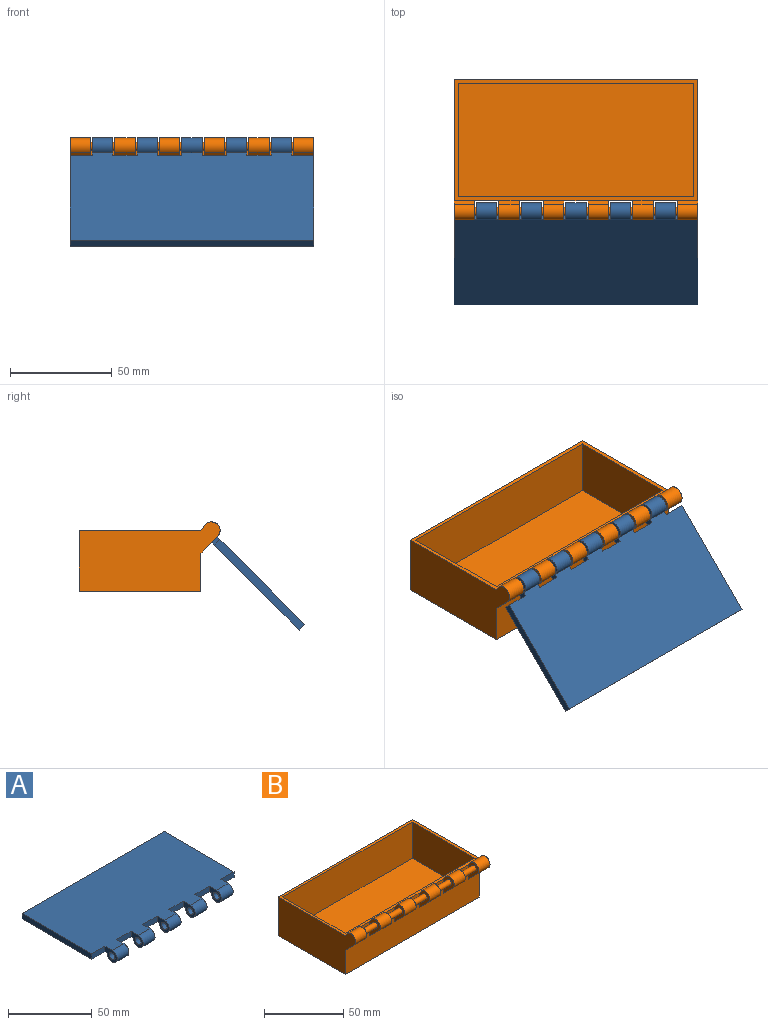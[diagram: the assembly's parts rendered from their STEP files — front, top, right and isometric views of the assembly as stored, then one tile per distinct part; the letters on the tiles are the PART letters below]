
ASSEMBLY  parts=2 mates=1
PART A: 31 faces, bbox 120x69.4x8.4 mm
  f0: plane 10.27x8.4mm, normal (1,0,0), area 48.6mm2, adj f2,f3,f4,f5,f11
  f1: plane 10.27x8.4mm, normal (-1,0,0), area 48.6mm2, adj f2,f3,f4,f5,f6
  f2: plane 120x65.2mm, normal (0,0,1), area 7399.1mm2, adj f0,f1,f3,f6,f7,f8,f9,f11
  f3: cylinder r=4.2mm len=10mm, axis (-1,0,0), area 199.9mm2, adj f0,f1,f2,f4
  f4: plane 120x61mm, normal (0,0,-1), area 7189.4mm2, adj f0,f1,f3,f6,f7,f8,f9,f11
  f5: cylinder r=2.4mm len=10mm, axis (-1,0,0), area 150.8mm2, adj f0,f1
  f6: plane 11x4mm, normal (0,-1,0), area 44mm2, adj f1,f2,f4,f29
  f7: plane 10.27x8.4mm, normal (1,0,0), area 48.6mm2, adj f2,f4,f9,f10,f16
  f8: plane 10.27x8.4mm, normal (-1,0,0), area 48.6mm2, adj f2,f4,f9,f10,f11
  f9: cylinder r=4.2mm len=10mm, axis (-1,0,0), area 199.9mm2, adj f2,f4,f7,f8
  f10: cylinder r=2.4mm len=10mm, axis (-1,0,0), area 150.8mm2, adj f7,f8
  f11: plane 12x4mm, normal (0,-1,0), area 48mm2, adj f0,f2,f4,f8
  f12: plane 10.27x8.4mm, normal (1,0,0), area 48.6mm2, adj f2,f4,f14,f15,f21
  f13: plane 10.27x8.4mm, normal (-1,0,0), area 48.6mm2, adj f2,f4,f14,f15,f16
  f14: cylinder r=4.2mm len=10mm, axis (-1,0,0), area 199.9mm2, adj f2,f4,f12,f13
  f15: cylinder r=2.4mm len=10mm, axis (-1,0,0), area 150.8mm2, adj f12,f13
  f16: plane 12x4mm, normal (0,-1,0), area 48mm2, adj f2,f4,f7,f13
  f17: plane 10.27x8.4mm, normal (1,0,0), area 48.6mm2, adj f2,f4,f19,f20,f26
  f18: plane 10.27x8.4mm, normal (-1,0,0), area 48.6mm2, adj f2,f4,f19,f20,f21
  f19: cylinder r=4.2mm len=10mm, axis (-1,0,0), area 199.9mm2, adj f2,f4,f17,f18
  f20: cylinder r=2.4mm len=10mm, axis (-1,0,0), area 150.8mm2, adj f17,f18
  f21: plane 12x4mm, normal (0,-1,0), area 48mm2, adj f2,f4,f12,f18
  f22: plane 10.27x8.4mm, normal (1,0,0), area 48.6mm2, adj f2,f4,f24,f25,f28
  f23: plane 10.27x8.4mm, normal (-1,0,0), area 48.6mm2, adj f2,f4,f24,f25,f26
  f24: cylinder r=4.2mm len=10mm, axis (-1,0,0), area 199.9mm2, adj f2,f4,f22,f23
  f25: cylinder r=2.4mm len=10mm, axis (-1,0,0), area 150.8mm2, adj f22,f23
  f26: plane 12x4mm, normal (0,-1,0), area 48mm2, adj f2,f4,f17,f23
  f27: plane 59.13x4mm, normal (1,0,0), area 236.5mm2, adj f2,f4,f28,f30
  f28: plane 11x4mm, normal (0,-1,0), area 44mm2, adj f2,f4,f22,f27
  f29: plane 59.13x4mm, normal (-1,0,0), area 236.5mm2, adj f2,f4,f6,f30
  f30: plane 120x4mm, normal (0,1,0), area 480mm2, adj f2,f4,f27,f29
PART B: 44 faces, bbox 120x69.4x34.2 mm
  f0: plane 120x30mm, normal (0,-1,0), area 2931.6mm2, adj f1,f2,f4,f5,f12,f14,f18,f20
  f1: plane 120x60mm, normal (0,0,1), area 704mm2, adj f0,f2,f3,f4,f6,f7,f8,f9
  f2: plane 69.4x34.2mm, normal (1,0,0), area 1888.7mm2, adj f0,f1,f3,f5,f11,f12,f13
  f3: plane 120x30mm, normal (0,1,0), area 3600mm2, adj f1,f2,f4,f5
  f4: plane 69.4x34.2mm, normal (-1,0,0), area 1888.7mm2, adj f0,f1,f3,f5,f40,f41,f42
  f5: plane 120x60mm, normal (0,0,-1), area 7200mm2, adj f0,f2,f3,f4
  f6: plane 116x28mm, normal (0,1,0), area 3248mm2, adj f1,f7,f9,f10
  f7: plane 56x28mm, normal (-1,0,0), area 1568mm2, adj f1,f6,f8,f10
  f8: plane 116x28mm, normal (0,-1,0), area 3248mm2, adj f1,f7,f9,f10
  f9: plane 56x28mm, normal (1,0,0), area 1568mm2, adj f1,f6,f8,f10
  f10: plane 116x56mm, normal (0,0,1), area 6496mm2, adj f6,f7,f8,f9
  f11: cylinder r=4.2mm len=10mm, axis (1,0,0), area 138.4mm2, adj f2,f12,f13,f14
  f12: plane 10x8.17mm, normal (0,-0.71,-0.71), area 115.5mm2, adj f0,f2,f11,f14
  f13: plane 10x2.48mm, normal (0,0.81,0.59), area 30.7mm2, adj f1,f2,f11,f14
  f14: plane 15.34x9.4mm, normal (-1,0,0), area 76.2mm2, adj f0,f11,f12,f13,f15
  f15: cylinder r=2mm len=12mm, axis (1,0,0), area 150.8mm2, adj f14,f21
  f16: cylinder r=2mm len=12mm, axis (1,0,0), area 150.8mm2, adj f20,f26
  f17: cylinder r=4.2mm len=10mm, axis (1,0,0), area 138.4mm2, adj f18,f19,f20,f21
  f18: plane 10x8.17mm, normal (0,-0.71,-0.71), area 115.5mm2, adj f0,f17,f20,f21
  f19: plane 10x2.48mm, normal (0,0.81,0.59), area 30.7mm2, adj f1,f17,f20,f21
  f20: plane 15.34x9.4mm, normal (-1,0,0), area 76.2mm2, adj f0,f16,f17,f18,f19
  f21: plane 15.34x9.4mm, normal (1,0,0), area 76.2mm2, adj f0,f15,f17,f18,f19
  f22: cylinder r=4.2mm len=10mm, axis (1,0,0), area 138.4mm2, adj f23,f24,f25,f26
  f23: plane 10x8.17mm, normal (0,-0.71,-0.71), area 115.5mm2, adj f0,f22,f25,f26
  f24: plane 10x2.48mm, normal (0,0.81,0.59), area 30.7mm2, adj f1,f22,f25,f26
  f25: plane 15.34x9.4mm, normal (-1,0,0), area 76.2mm2, adj f0,f22,f23,f24,f27
  f26: plane 15.34x9.4mm, normal (1,0,0), area 76.2mm2, adj f0,f16,f22,f23,f24
  f27: cylinder r=2mm len=12mm, axis (1,0,0), area 150.8mm2, adj f25,f32
  f28: cylinder r=4.2mm len=10mm, axis (1,0,0), area 138.4mm2, adj f29,f30,f31,f32
  f29: plane 10x8.17mm, normal (0,-0.71,-0.71), area 115.5mm2, adj f0,f28,f31,f32
  f30: plane 10x2.48mm, normal (0,0.81,0.59), area 30.7mm2, adj f1,f28,f31,f32
  f31: plane 15.34x9.4mm, normal (-1,0,0), area 76.2mm2, adj f0,f28,f29,f30,f33
  f32: plane 15.34x9.4mm, normal (1,0,0), area 76.2mm2, adj f0,f27,f28,f29,f30
  f33: cylinder r=2mm len=12mm, axis (1,0,0), area 150.8mm2, adj f31,f38
  f34: cylinder r=4.2mm len=10mm, axis (1,0,0), area 138.4mm2, adj f35,f36,f37,f38
  f35: plane 10x8.17mm, normal (0,-0.71,-0.71), area 115.5mm2, adj f0,f34,f37,f38
  f36: plane 10x2.48mm, normal (0,0.81,0.59), area 30.7mm2, adj f1,f34,f37,f38
  f37: plane 15.34x9.4mm, normal (-1,0,0), area 76.2mm2, adj f0,f34,f35,f36,f39
  f38: plane 15.34x9.4mm, normal (1,0,0), area 76.2mm2, adj f0,f33,f34,f35,f36
  f39: cylinder r=2mm len=12mm, axis (1,0,0), area 150.8mm2, adj f37,f43
  f40: cylinder r=4.2mm len=10mm, axis (1,0,0), area 138.4mm2, adj f4,f41,f42,f43
  f41: plane 10x8.17mm, normal (0,-0.71,-0.71), area 115.5mm2, adj f0,f4,f40,f43
  f42: plane 10x2.48mm, normal (0,0.81,0.59), area 30.7mm2, adj f1,f4,f40,f43
  f43: plane 15.34x9.4mm, normal (1,0,0), area 76.2mm2, adj f0,f39,f40,f41,f42
PLACE A rot(axis=(-1,0,0),135deg) t=(47.41,-20.2,38.22)mm
PLACE B t=(47.41,-20.2,38.22)mm
MATE revolute A.f5 <-> B.f11  axis (1,0,0) through (47.41,-20.2,38.22)mm
